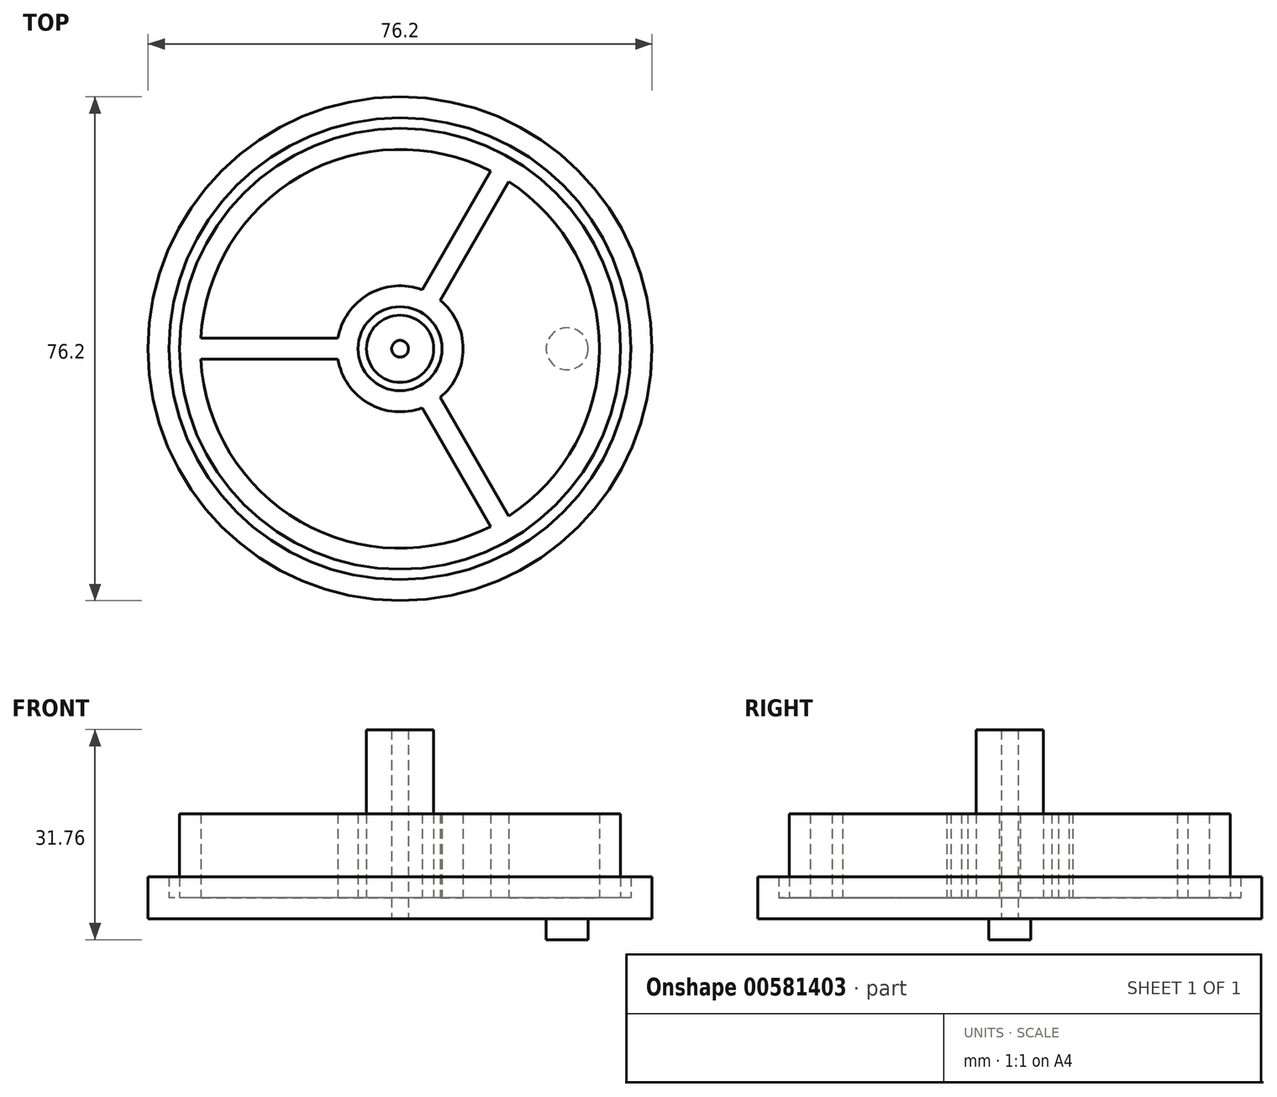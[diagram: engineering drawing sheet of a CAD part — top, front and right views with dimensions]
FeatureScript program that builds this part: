
annotation { "Feature Type Name" : "Feature", "Feature Type Description" : "" }
export const myFeature = defineFeature(function(context is Context, id is Id, definition is map)
    precondition{}
    {
        {
            var Q0;
            Q0=qCreatedBy(makeId("Top.planeOp"),FACE);
            var sketch = newSketch(context, id + "F0", { "sketchPlane" : qUnion([Q0])});
            skCircle(sketch, "E0", {"center": v(0, 0) * mm, "radius": 38.1 * mm});
            skCircle(sketch, "E1", {"center": v(0, 0) * mm, "radius": 1.27 * mm});
            skCircle(sketch, "E2", {"center": v(25.27, 0) * mm, "radius": 3.18 * mm});
            skSolve(sketch);
        }
        {
            var Q0;
            Q0=makeQuery(id+"F0.imprint","IMPRINT",FACE,{"disambiguationData":[TD([[makeQuery(id+"F0.imprint","IMPRINT",EDGE,{"derivedFrom":sQuery(id+"F0.wireOp",EDGE,"E0")}),1.0]])]});
            var Q1;
            Q1=makeQuery(id+"F0.imprint","IMPRINT",FACE,{"disambiguationData":[TD([[makeQuery(id+"F0.imprint","IMPRINT",EDGE,{"derivedFrom":sQuery(id+"F0.wireOp",EDGE,"E2")}),1.0]])]});
            var Q2;
            Q2=makeQuery(id+"F0.imprint","IMPRINT",FACE,{"disambiguationData":[TD([[makeQuery(id+"F0.imprint","IMPRINT",EDGE,{"derivedFrom":sQuery(id+"F0.wireOp",EDGE,"E1")}),1.0]])]});
            extrude(context, id + "F1", {"entities" : qUnion([Q0, Q1, Q2]), "depth" : 3.17 * mm, "offsetDistance" : 25.4 * mm});
        }
        {
            var Q0;
            Q0=makeQuery(id+"F0.imprint","IMPRINT",FACE,{"disambiguationData":[TD([[makeQuery(id+"F0.imprint","IMPRINT",EDGE,{"derivedFrom":sQuery(id+"F0.wireOp",EDGE,"E2")}),1.0]])]});
            extrude(context, id + "F2", {"entities" : qUnion([Q0]), "operationType" : NewBodyOperationType.ADD, "oppositeDirection" : true, "depth" : 3.17 * mm, "offsetDistance" : 25.4 * mm});
        }
        {
            var Q0;
            Q0=makeQuery(id+"F0.imprint","IMPRINT",FACE,{"disambiguationData":[TD([[makeQuery(id+"F0.imprint","IMPRINT",EDGE,{"derivedFrom":sQuery(id+"F0.wireOp",EDGE,"E1")}),1.0]])]});
            extrude(context, id + "F3", {"entities" : qUnion([Q0]), "operationType" : NewBodyOperationType.REMOVE, "endBound" : BoundingType.UP_TO_NEXT, "depth" : 25.4 * mm, "offsetDistance" : 25.4 * mm});
        }
        {
            var Q0;
            Q0=makeQuery(id+"F1.opExtrude","CAP_FACE",FACE,{"disambiguationData":[OSD([sQuery(id+"F0.wireOp",EDGE,"E0")])],"isStart":false});
            var sketch = newSketch(context, id + "F4", { "sketchPlane" : qUnion([Q0])});
            skCircle(sketch, "E3", {"center": v(0, 0) * mm, "radius": 34.93 * mm});
            skSolve(sketch);
        }
        {
            var Q0;
            Q0=makeQuery(id+"F4.imprint","IMPRINT",FACE,{"disambiguationData":[TD([[makeQuery(id+"F4.imprint","IMPRINT",EDGE,{"derivedFrom":sQuery(id+"F4.wireOp",EDGE,"E3")}),-1.0]])]});
            extrude(context, id + "F5", {"entities" : qUnion([Q0]), "operationType" : NewBodyOperationType.ADD, "depth" : 3.17 * mm, "offsetDistance" : 25.4 * mm});
        }
        {
            var Q0;
            Q0=makeQuery(id+"F1.opExtrude","CAP_FACE",FACE,{"disambiguationData":[OSD([sQuery(id+"F0.wireOp",EDGE,"E0")])],"isStart":false});
            var sketch = newSketch(context, id + "F6", { "sketchPlane" : qUnion([Q0])});
            skCircle(sketch, "E4", {"center": v(0, 0) * mm, "radius": 33.34 * mm});
            skArc(sketch, "E5", {"start": v(-9.4, -1.59) * mm, "mid": v(-4.76, -8.25) * mm, "end": v(3.32, -8.93) * mm});
            skLineSegment(sketch, "E6", {"start": v(-30.12, 1.59) * mm, "end": v(-9.4, 1.59) * mm});
            skLineSegment(sketch, "E7", {"start": v(-30.12, -1.59) * mm, "end": v(-9.4, -1.59) * mm});
            skLineSegment(sketch, "E8.1.0", {"start": v(13.69, -26.88) * mm, "end": v(3.32, -8.93) * mm});
            skLineSegment(sketch, "E8.1.1", {"start": v(16.44, -25.3) * mm, "end": v(6.07, -7.34) * mm});
            skLineSegment(sketch, "E8.2.0", {"start": v(16.44, 25.3) * mm, "end": v(6.07, 7.34) * mm});
            skLineSegment(sketch, "E8.2.1", {"start": v(13.69, 26.88) * mm, "end": v(3.32, 8.93) * mm});
            skCircle(sketch, "E9", {"center": v(0, 0) * mm, "radius": 6.35 * mm});
            skArc(sketch, "E10", {"start": v(-30.12, -1.59) * mm, "mid": v(-15.08, -26.12) * mm, "end": v(13.69, -26.88) * mm});
            skPoint(sketch, "E11.orphan", {"position": v(15.28, -29.63) * mm});
            skPoint(sketch, "E12.orphan", {"position": v(18.02, -28.04) * mm});
            skPoint(sketch, "E13.orphan", {"position": v(18.02, 28.04) * mm});
            skPoint(sketch, "E14.orphan", {"position": v(15.28, 29.63) * mm});
            skPoint(sketch, "E15.orphan", {"position": v(-33.3, 1.59) * mm});
            skPoint(sketch, "E16.orphan", {"position": v(-33.3, -1.59) * mm});
            skArc(sketch, "E17.trimOffspring", {"start": v(3.32, 8.93) * mm, "mid": v(-4.76, 8.25) * mm, "end": v(-9.4, 1.59) * mm});
            skArc(sketch, "E18.trimOffspring", {"start": v(13.69, 26.88) * mm, "mid": v(-15.08, 26.12) * mm, "end": v(-30.12, 1.59) * mm});
            skArc(sketch, "E19.trimOffspring", {"start": v(6.07, -7.34) * mm, "mid": v(9.53, 0) * mm, "end": v(6.07, 7.34) * mm});
            skArc(sketch, "E20.trimOffspring", {"start": v(16.44, -25.3) * mm, "mid": v(30.16, 0) * mm, "end": v(16.44, 25.3) * mm});
            skSolve(sketch);
        }
        {
            var Q0;
            {var subQ0=sQuery(id+"F6.wireOp",EDGE,"E8.2.0");Q0=makeQuery(id+"F6.imprint","IMPRINT",FACE,{"disambiguationData":[TD([[makeQuery(id+"F6.imprint","IMPRINT",EDGE,{"derivedFrom":subQ0}),-1.0]])]});}
            var Q1;
            {var subQ0=sQuery(id+"F6.wireOp",EDGE,"E8.1.0");Q1=makeQuery(id+"F6.imprint","IMPRINT",FACE,{"disambiguationData":[TD([[makeQuery(id+"F6.imprint","IMPRINT",EDGE,{"derivedFrom":subQ0}),-1.0]])]});}
            var Q2;
            Q2=makeQuery(id+"F6.imprint","IMPRINT",FACE,{"disambiguationData":[TD([[makeQuery(id+"F6.imprint","IMPRINT",EDGE,{"derivedFrom":makeQuery(id+"FgqhglRRKZOeuim_1.opExtrude","CAP_EDGE",EDGE,{"disambiguationData":[OSD([sQuery(id+"FpUWMTmtolLC9Im_1.wireOp",EDGE,"BoEegt8j-Iarj-6F5e-RcIg-200uzfAPz9b4")])],"isStart":true})}),1.0]])]});
            var Q3;
            {var subQ0=sQuery(id+"F6.wireOp",EDGE,"E6");Q3=makeQuery(id+"F6.imprint","IMPRINT",FACE,{"disambiguationData":[TD([[makeQuery(id+"F6.imprint","IMPRINT",EDGE,{"derivedFrom":subQ0}),-1.0]])]});}
            var Q4;
            Q4=makeQuery(id+"F6.imprint","IMPRINT",FACE,{"disambiguationData":[TD([[makeQuery(id+"F6.imprint","IMPRINT",EDGE,{"derivedFrom":sQuery(id+"F6.wireOp",EDGE,"E9")}),-1.0]])]});
            extrude(context, id + "F7", {"entities" : qUnion([Q0, Q1, Q2, Q3, Q4]), "depth" : 12.7 * mm, "offsetDistance" : 25.4 * mm});
        }
        {
            var Q0;
            Q0=makeQuery(id+"F1.opExtrude","CAP_FACE",FACE,{"disambiguationData":[OSD([sQuery(id+"F0.wireOp",EDGE,"E0")])],"isStart":false});
            var sketch = newSketch(context, id + "F8", { "sketchPlane" : qUnion([Q0])});
            skCircle(sketch, "E21", {"center": v(0, 0) * mm, "radius": 5.08 * mm});
            skCircle(sketch, "E22.0", {"center": v(0, 0) * mm, "radius": 1.27 * mm});
            skSolve(sketch);
        }
        {
            var Q0;
            Q0=makeQuery(id+"F8.imprint","IMPRINT",FACE,{"disambiguationData":[TD([[makeQuery(id+"F8.imprint","IMPRINT",EDGE,{"derivedFrom":sQuery(id+"F8.wireOp",EDGE,"E21")}),1.0]])]});
            extrude(context, id + "F9", {"entities" : qUnion([Q0]), "depth" : 25.4 * mm, "offsetDistance" : 25.4 * mm});
        }
    });
